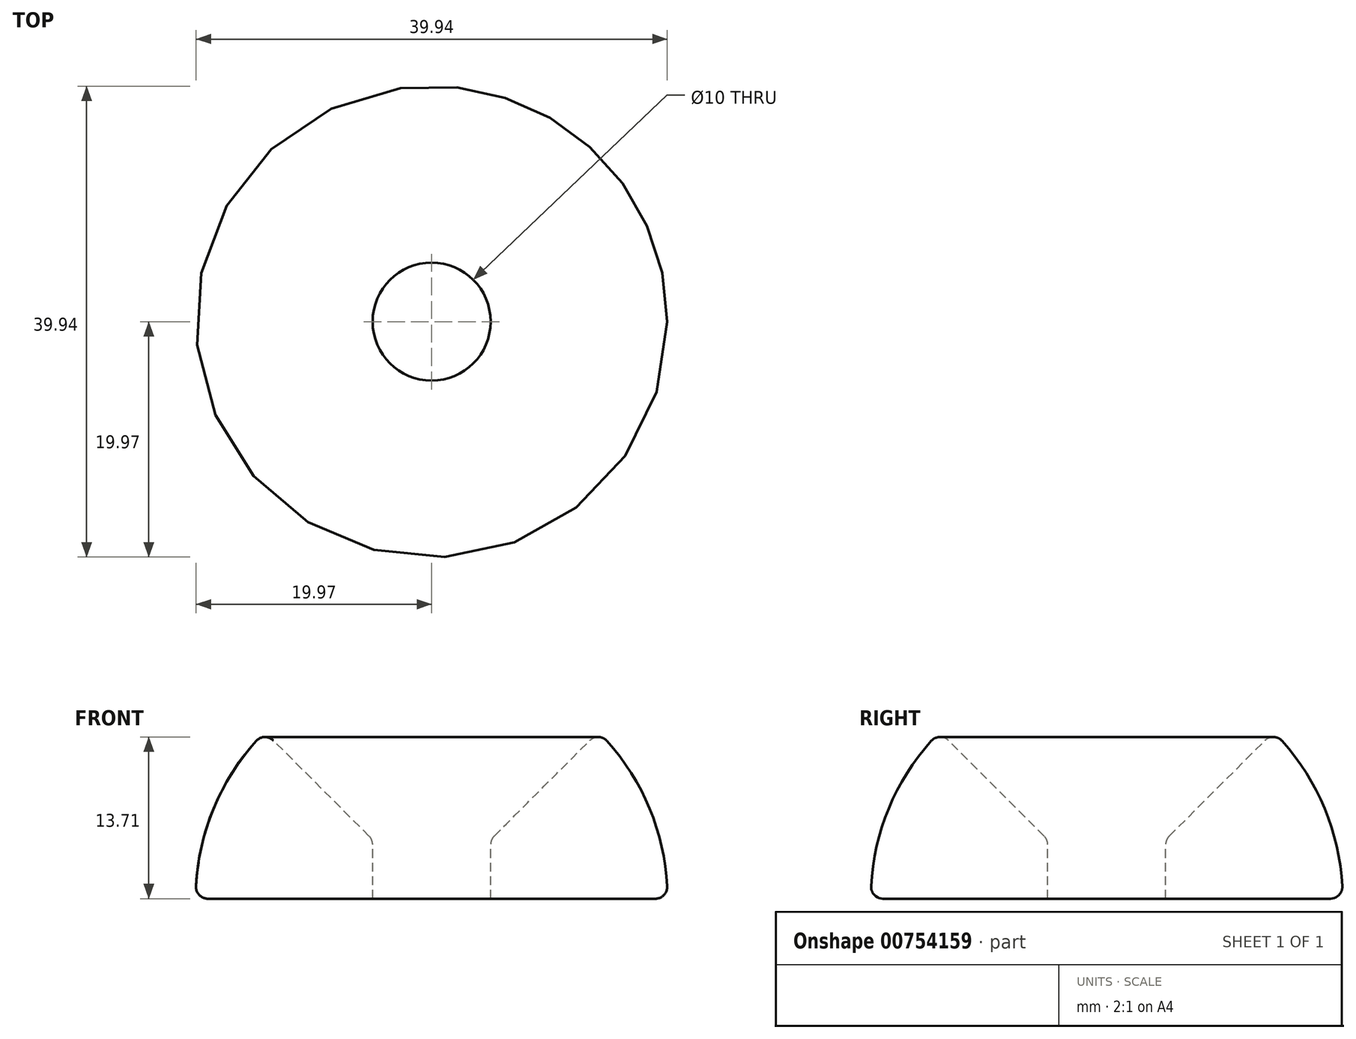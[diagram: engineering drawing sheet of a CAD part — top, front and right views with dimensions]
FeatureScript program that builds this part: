
annotation { "Feature Type Name" : "Feature", "Feature Type Description" : "" }
export const myFeature = defineFeature(function(context is Context, id is Id, definition is map)
    precondition{}
    {
        {
            var Q0;
            Q0=qCreatedBy(makeId("Front.planeOp"),FACE);
            var sketch = newSketch(context, id + "F0", { "sketchPlane" : qUnion([Q0])});
            skLineSegment(sketch, "E0", {"start": v(0, 31.88) * mm, "end": v(0, -28.89) * mm});
            skArc(sketch, "E1", {"start": v(0, -20) * mm, "mid": v(20, 0) * mm, "end": v(0, 20) * mm});
            skLineSegment(sketch, "E2", {"start": v(0, 0) * mm, "end": v(20, 0) * mm});
            skLineSegment(sketch, "E3", {"start": v(0, 0) * mm, "end": v(5, 0) * mm});
            skLineSegment(sketch, "E4", {"start": v(5, 0) * mm, "end": v(5, 5) * mm});
            skLineSegment(sketch, "E5", {"start": v(5, 5) * mm, "end": v(14.14, 14.14) * mm});
            skSolve(sketch);
        }
        {
            var Q0;
            {var subQ0=sQuery(id+"F0.wireOp",EDGE,"E2");Q0=makeQuery(id+"F0.imprint","IMPRINT",FACE,{"disambiguationData":[TD([[makeQuery(id+"F0.imprint","IMPRINT",EDGE,{"derivedFrom":subQ0}),1.0]])]});}
            var Q1;
            Q1=sQuery(id+"F0.wireOp",EDGE,"E0");
            revolve(context, id + "F1", {"surfaceOperationType" : NewSurfaceOperationType.NEW, "entities" : qUnion([Q0]), "axis" : qUnion([Q1]), "revolveType" : RevolveType.FULL});
        }
        {
            var Q0;
            Q0=makeQuery(id+"F1.opRevolve","SWEPT_EDGE",EDGE,{"disambiguationData":[OSD([sQuery(id+"F0.wireOp",EDGE,"E1"),sQuery(id+"F0.wireOp",EDGE,"sR14CHAb-Lljj-xafI-cTfW-3jdyRtwucZpS")])]});
            var Q1;
            Q1=makeQuery(id+"F1.opRevolve","SWEPT_EDGE",EDGE,{"disambiguationData":[OSD([sQuery(id+"F0.wireOp",EDGE,"E4"),sQuery(id+"F0.wireOp",EDGE,"E5")])]});
            fillet(context, id + "F2", {"entities" : qUnion([Q0, Q1]), "radius" : 1 * mm, "tangentPropagation" : true, "allowEdgeOverflow" : false});
        }
    });
